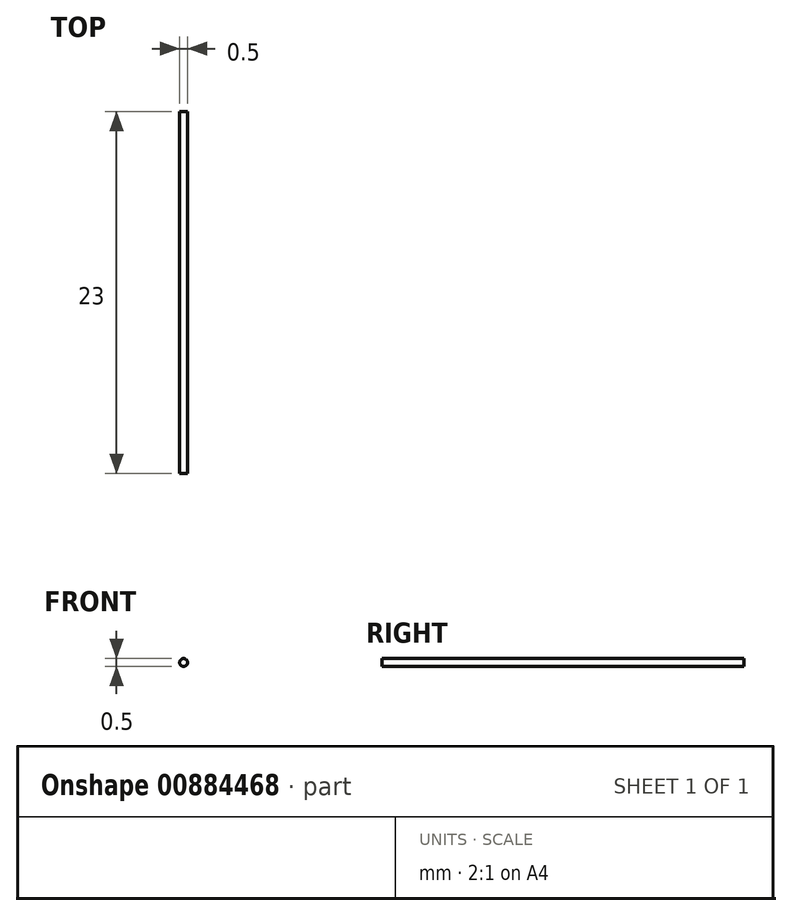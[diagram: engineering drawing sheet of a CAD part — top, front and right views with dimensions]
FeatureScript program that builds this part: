
annotation { "Feature Type Name" : "Feature", "Feature Type Description" : "" }
export const myFeature = defineFeature(function(context is Context, id is Id, definition is map)
    precondition{}
    {
        {
            var Q0;
            Q0=qCreatedBy(makeId("Front.planeOp"),FACE);
            var sketch = newSketch(context, id + "F0", { "sketchPlane" : qUnion([Q0])});
            skCircle(sketch, "E0", {"center": v(0, 0) * mm, "radius": 0.25 * mm});
            skSolve(sketch);
        }
        {
            var Q0;
            Q0=makeQuery(id+"F0.imprint","IMPRINT",FACE,{"disambiguationData":[TD([[makeQuery(id+"F0.imprint","IMPRINT",EDGE,{"derivedFrom":sQuery(id+"F0.wireOp",EDGE,"E0")}),1.0]])]});
            extrude(context, id + "F1", {"entities" : qUnion([Q0]), "depth" : 23 * mm, "offsetDistance" : 25 * mm});
        }
    });
